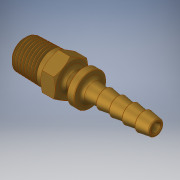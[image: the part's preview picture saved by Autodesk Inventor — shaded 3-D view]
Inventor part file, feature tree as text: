
AUTODESK INVENTOR PART (.ipt)
format: ipt  version: 2018 (Build 220112000, 112)  size: 778,752 bytes
history: native  units: in
note: dims shown in document units (in); Inventor stores cm internally (conversion verified against a paired STEP export)
features: extrude x1
ambient origin geometry x8: Origin, YZ Plane, XZ Plane, XY Plane, X Axis, Y Axis, Z Axis, Center Point
bodies: Solid1 (feature_tree)
feature tree (1):
  extrude  "Extrude1"  [1 undecoded]
note: 1 required parameter value undecoded (feature->parameter linkage not recoverable at this tier; creation-order binding heuristic only, values carry confidence <= 0.55)
